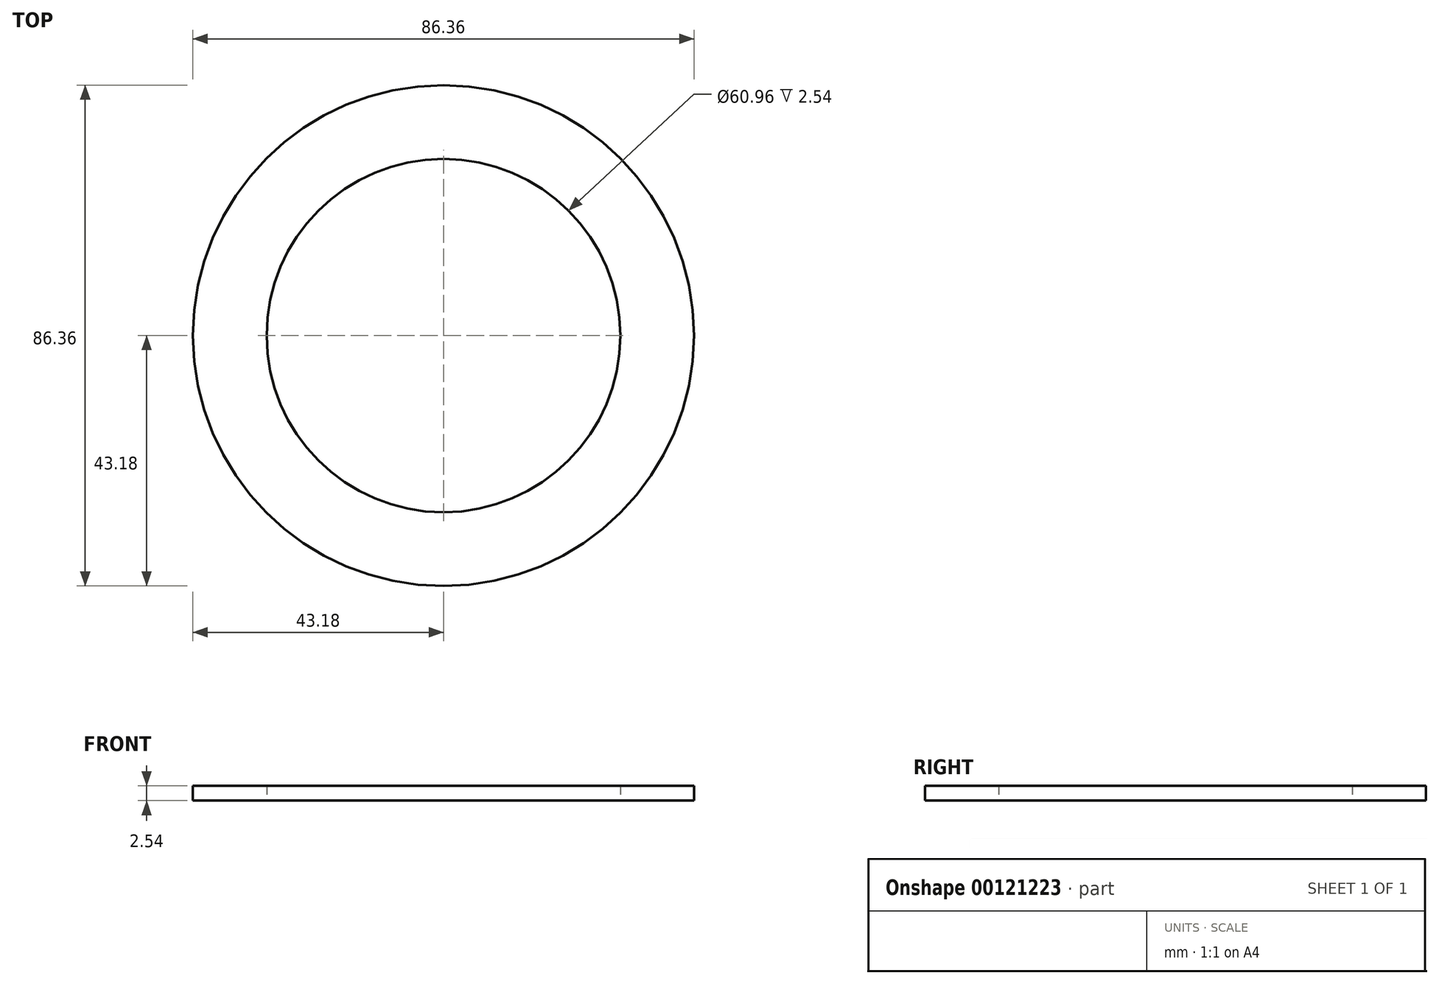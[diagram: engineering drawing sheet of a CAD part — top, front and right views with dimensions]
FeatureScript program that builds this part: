
annotation { "Feature Type Name" : "Feature", "Feature Type Description" : "" }
export const myFeature = defineFeature(function(context is Context, id is Id, definition is map)
    precondition{}
    {
        {
            var Q0;
            Q0=qCreatedBy(makeId("Top.planeOp"),FACE);
            var sketch = newSketch(context, id + "F0", { "sketchPlane" : qUnion([Q0])});
            skCircle(sketch, "E0", {"center": v(0, 0) * mm, "radius": 43.18 * mm});
            skCircle(sketch, "E1", {"center": v(0, 0) * mm, "radius": 30.48 * mm});
            skSolve(sketch);
        }
        {
            var Q0;
            Q0=makeQuery(id+"F0.imprint","IMPRINT",FACE,{"disambiguationData":[TD([[makeQuery(id+"F0.imprint","IMPRINT",EDGE,{"derivedFrom":sQuery(id+"F0.wireOp",EDGE,"E0")}),1.0]])]});
            extrude(context, id + "F1", {"entities" : qUnion([Q0]), "depth" : 2.54 * mm});
        }
    });
